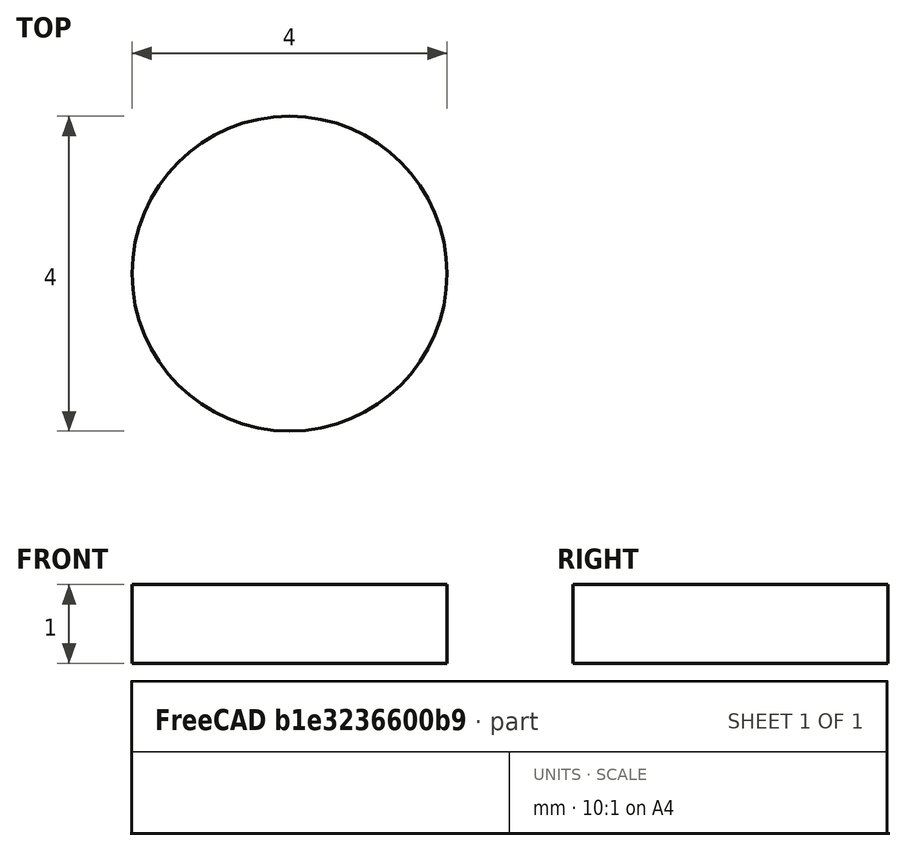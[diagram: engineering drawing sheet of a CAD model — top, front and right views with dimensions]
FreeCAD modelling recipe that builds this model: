
FCSTD DOCUMENT  (FreeCAD 1.1R44874 (Git))
Label: external-file
License: All rights reserved
LicenseURL: https://en.wikipedia.org/wiki/All_rights_reserved
objects: App::Point×3, App::Part×3, Part::Cylinder×1, App::LinkGroupPython×1, App::Link×1
note: 1 computed .brp shape members not serialized (recipe doc carries the construction recipe); baked Part::Feature solids carry a one-line shape summary decoded from their .brp
EXTERNAL_REF file=external-file2.FCStd obj=Part

FEATURE [Part::Cylinder] Cylinder
  Angle = 360
  AttacherType = Attacher::AttachEngine3D
  FirstAngle = 0
  Height = 1
  Radius = 2
  SecondAngle = 0
FEATURE [App::LinkGroupPython] OpticalMirrorGroup  label="linkedMirrorGroup"  # WARN: FeaturePython — macro-defined, semantics opaque (R4)
  AbsorptionLength = inf
  ElementList = -> [Cylinder]
  GratingDiffractionOrder = 1
  GratingLinesOrientation = (0,0,1)
  GratingLinesPerMillimeter = 1000
  GratingType = 0
  LinkMode = 0
  ModifyPhiDomain = 0, 2*pi
  ModifyThetaDomain = -pi/2, pi/2
  OpticalType = 0
  PowerPhiDomain = 0, 2*pi
  PowerThetaDomain = -pi/2, pi/2
  RecordHits = false
  Reflectivity = 1
  RefractiveIndex = 2
FEATURE [App::Point] Origin001
  Role = Origin
FEATURE [App::Part] Part001
  Group = -> [OpticalMirrorGroup]
  Origin = -> Origin002
  Placement = pos=(0,0,-25) rot=(0,0,1;0rad)
FEATURE [App::Part] Part
  Group = -> [Part001]
  Origin = -> Origin
FEATURE [App::Point] Origin003
  Role = Origin
FEATURE [App::Point] Origin005  label="Origin006"
  Role = Origin
FEATURE [App::Link] Link
  LinkedObject = -> <external external-file2.FCStd>#Part
FEATURE [App::Part] Part002  label="link-lens"
  Group = -> [Link]
  Origin = -> Origin004

RESOLVED EXTERNAL PARTS (link-assembly join: the EXTERNAL_REF files above that resolve inside this repo's crawl, each included once):
---- part external-file2.FCStd = doc fcstd_2f1645f87d6c ----
FCSTD DOCUMENT  (FreeCAD 1.1R44874 (Git))
Label: external-file2
License: All rights reserved
LicenseURL: https://en.wikipedia.org/wiki/All_rights_reserved
objects: Part::Sphere×2, Part::Cylinder×1, Part::MultiCommon×1, App::Point×1, App::LinkGroupPython×1, App::Part×1
note: 4 computed .brp shape members not serialized (recipe doc carries the construction recipe); baked Part::Feature solids carry a one-line shape summary decoded from their .brp

FEATURE [Part::Sphere] Sphere
  Angle1 = -90
  Angle2 = 90
  Angle3 = 360
  AttacherType = Attacher::AttachEngine3D
  Placement = pos=(0,0,-2) rot=(0,0,1;0rad)
  Radius = 5
FEATURE [Part::Sphere] Sphere001
  Angle1 = -90
  Angle2 = 90
  Angle3 = 360
  AttacherType = Attacher::AttachEngine3D
  Placement = pos=(0,0,7) rot=(0,0,1;0rad)
  Radius = 5
FEATURE [Part::Cylinder] Cylinder
  Angle = 360
  AttacherType = Attacher::AttachEngine3D
  FirstAngle = 0
  Height = 10
  Placement = pos=(0,0,-3) rot=(0,0,1;0rad)
  Radius = 2
  SecondAngle = 0
FEATURE [Part::MultiCommon] Common
  Behavior = 0
  Refine = true
  Shapes = -> [Sphere,Sphere001,Cylinder]
FEATURE [App::Point] Origin001
  Role = Origin
FEATURE [App::LinkGroupPython] OpticalLensGroup  # WARN: FeaturePython — macro-defined, semantics opaque (R4)
  AbsorptionLength = inf
  ElementList = -> [Common]
  GratingDiffractionOrder = 1
  GratingLinesOrientation = (0,0,1)
  GratingLinesPerMillimeter = 1000
  GratingType = 0
  LinkMode = 0
  ModifyPhiDomain = 0, 2*pi
  ModifyThetaDomain = -pi/2, pi/2
  OpticalType = 1
  Placement = pos=(0,0,-2.5) rot=(0,0,1;0rad)
  PowerPhiDomain = 0, 2*pi
  PowerThetaDomain = -pi/2, pi/2
  RecordHits = false
  Reflectivity = 1
  RefractiveIndex = 1.4
FEATURE [App::Part] Part  label="spherical-lens"
  Group = -> [OpticalLensGroup]
  Origin = -> Origin
